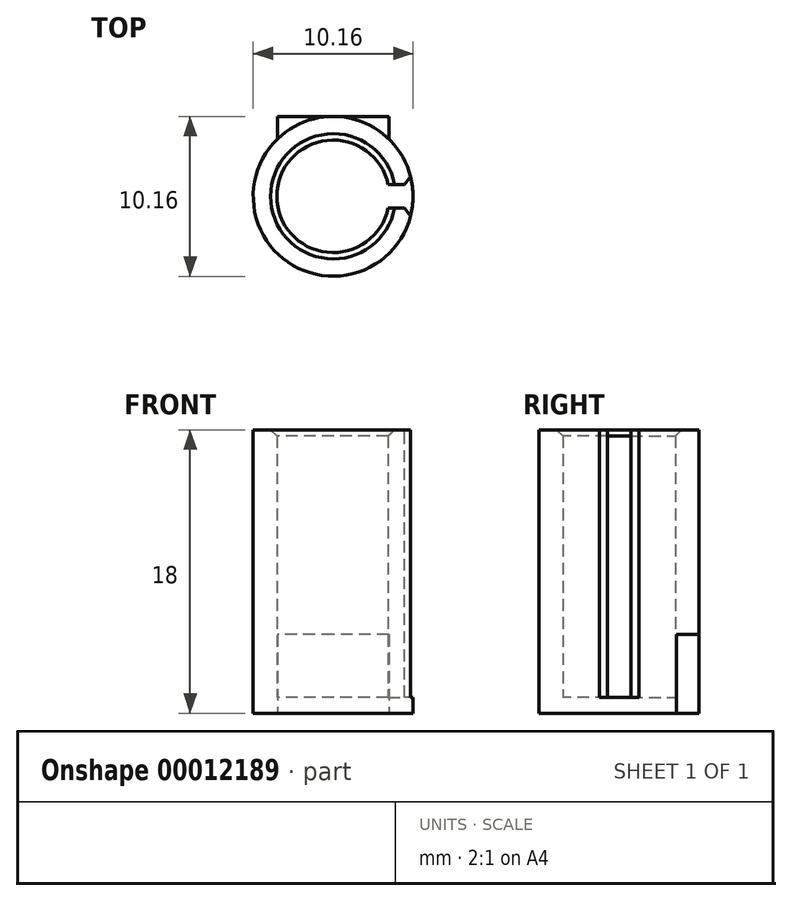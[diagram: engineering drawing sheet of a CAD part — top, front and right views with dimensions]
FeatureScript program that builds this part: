
annotation { "Feature Type Name" : "Feature", "Feature Type Description" : "" }
export const myFeature = defineFeature(function(context is Context, id is Id, definition is map)
    precondition{}
    {
        {
            var Q0;
            Q0=qCreatedBy(makeId("Top.planeOp"),FACE);
            var sketch = newSketch(context, id + "F0", { "sketchPlane" : qUnion([Q0])});
            skCircle(sketch, "E0", {"center": v(0, 0) * mm, "radius": 3.58 * mm});
            skCircle(sketch, "E1", {"center": v(0, 0) * mm, "radius": 5.07 * mm});
            skLineSegment(sketch, "E2.right", {"start": v(3.5, 0.75) * mm, "end": v(5.02, 0.75) * mm});
            skLineSegment(sketch, "E3", {"start": v(0, 0) * mm, "end": v(5.02, 0) * mm, "construction": true});
            skLineSegment(sketch, "E4", {"start": v(0, 3.58) * mm, "end": v(0, 5.07) * mm, "construction": true});
            skPoint(sketch, "E5.rect.middle", {"position": v(-3.58, 0) * mm});
            skLineSegment(sketch, "E6.rect.bottom", {"start": v(3.54, 5.07) * mm, "end": v(-3.54, 5.07) * mm});
            skLineSegment(sketch, "E6.rect.left", {"start": v(3.54, 5.08) * mm, "end": v(3.54, 3.64) * mm});
            skLineSegment(sketch, "E6.rect.right", {"start": v(-3.54, 5.08) * mm, "end": v(-3.54, 3.64) * mm});
            skPoint(sketch, "E6.rect.middle", {"position": v(0, 5.07) * mm});
            skLineSegment(sketch, "E7", {"start": v(3.5, -0.75) * mm, "end": v(5.02, -0.75) * mm});
            skLineSegment(sketch, "E8", {"start": v(5.02, -0.75) * mm, "end": v(5.02, 0.75) * mm, "construction": true});
            skSolve(sketch);
        }
        {
            var Q0;
            {var subQ5=sQuery(id+"F0.wireOp",EDGE,"E2.right");Q0=makeQuery(id+"F0.imprint","IMPRINT",FACE,{"disambiguationData":[TD([[makeQuery(id+"F0.imprint","IMPRINT",EDGE,{"derivedFrom":subQ5}),1.0]])]});}
            extrude(context, id + "F1", {"entities" : qUnion([Q0]), "depth" : 18 * mm});
        }
        {
            var Q0;
            {var subQ0=sQuery(id+"F0.wireOp",EDGE,"E0");var subQ2=makeQuery(id+"F0.imprint","INTERSECT",VERTEX,{"derivedFrom":[subQ0,sQuery(id+"F0.wireOp",EDGE,"c1c1d53d-256f-4571-9a13-228adffb0879.right")]});Q0=makeQuery(id+"F0.imprint","IMPRINT",FACE,{"disambiguationData":[TD([[makeQuery(id+"F0.imprint","IMPRINT",EDGE,{"disambiguationData":[TD([[subQ2,-1.0]])],"derivedFrom":subQ0}),1.0]])]});}
            var Q1;
            {var subQ0=sQuery(id+"F0.wireOp",EDGE,"E6.rect.top");var subQ1=sQuery(id+"F0.wireOp",EDGE,"E0");var subQ3=makeQuery(id+"F0.imprint","INTERSECT",VERTEX,{"disambiguationData":[OD(0.0)],"derivedFrom":[subQ1,subQ0]});Q1=makeQuery(id+"F0.imprint","IMPRINT",FACE,{"disambiguationData":[TD([[makeQuery(id+"F0.imprint","IMPRINT",EDGE,{"disambiguationData":[TD([[subQ3,1.0]])],"derivedFrom":subQ1}),1.0]])]});}
            var Q2;
            {var subQ1=sQuery(id+"F0.wireOp",EDGE,"E2.right");Q2=makeQuery(id+"F0.imprint","IMPRINT",FACE,{"disambiguationData":[TD([[makeQuery(id+"F0.imprint","IMPRINT",EDGE,{"derivedFrom":subQ1}),-1.0]])]});}
            extrude(context, id + "F2", {"entities" : qUnion([Q0, Q1, Q2]), "operationType" : NewBodyOperationType.ADD, "depth" : 1 * mm});
        }
        {
            var Q0;
            {var subQ3=sQuery(id+"F0.wireOp",EDGE,"E6.rect.right");Q0=makeQuery(id+"F0.imprint","IMPRINT",FACE,{"disambiguationData":[TD([[makeQuery(id+"F0.imprint","IMPRINT",EDGE,{"derivedFrom":subQ3}),1.0]])]});}
            var Q1;
            {var subQ0=sQuery(id+"F0.wireOp",EDGE,"E6.rect.left");Q1=makeQuery(id+"F0.imprint","IMPRINT",FACE,{"disambiguationData":[TD([[makeQuery(id+"F0.imprint","IMPRINT",EDGE,{"derivedFrom":subQ0}),-1.0]])]});}
            extrude(context, id + "F3", {"entities" : qUnion([Q0, Q1]), "operationType" : NewBodyOperationType.ADD, "depth" : 5 * mm});
        }
        {
            var Q0;
            Q0=makeQuery(id+"F1.opExtrude","CAP_EDGE",EDGE,{"disambiguationData":[OSD([sQuery(id+"F0.wireOp",EDGE,"E0")])],"isStart":false});
            var Q1;
            Q1=makeQuery(id+"F1.opExtrude","SWEPT_EDGE",EDGE,{"disambiguationData":[OSD([sQuery(id+"F0.wireOp",EDGE,"E1"),sQuery(id+"F0.wireOp",EDGE,"c1c1d53d-256f-4571-9a13-228adffb0879.right")])]});
            var Q2;
            Q2=makeQuery(id+"F1.opExtrude","SWEPT_EDGE",EDGE,{"disambiguationData":[OSD([sQuery(id+"F0.wireOp",EDGE,"E1"),sQuery(id+"F0.wireOp",EDGE,"E2.right")])]});
            chamfer(context, id + "F4", {"entities" : qUnion([Q0, Q1, Q2]), "width" : .4 * mm, "tangentPropagation" : true});
        }
    });
